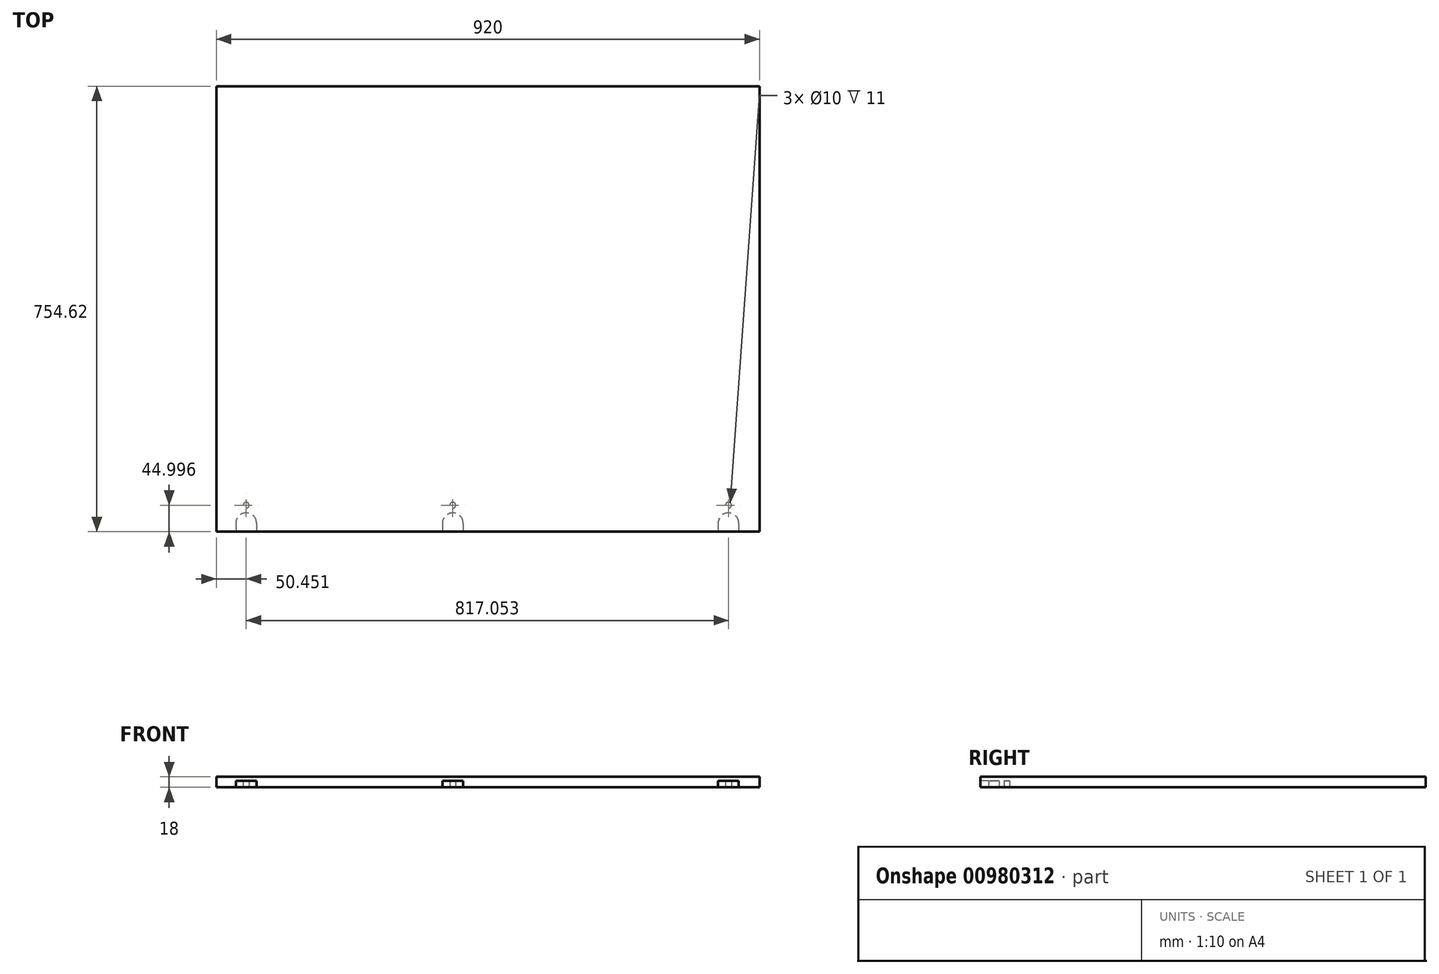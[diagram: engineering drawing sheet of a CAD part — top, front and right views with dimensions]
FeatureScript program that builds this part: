
annotation { "Feature Type Name" : "Feature", "Feature Type Description" : "" }
export const myFeature = defineFeature(function(context is Context, id is Id, definition is map)
    precondition{}
    {
        {
            var Q0;
            Q0=qCreatedBy(makeId("Top.planeOp"),FACE);
            var sketch = newSketch(context, id + "F0", { "sketchPlane" : qUnion([Q0])});
            skLineSegment(sketch, "E0.bottom", {"start": v(-458.88, 406.43) * mm, "end": v(461.12, 406.43) * mm});
            skLineSegment(sketch, "E0.top", {"start": v(-458.88, -348.2) * mm, "end": v(-425.83, -348.2) * mm});
            skLineSegment(sketch, "E0.left", {"start": v(-458.88, 406.43) * mm, "end": v(-458.88, -348.2) * mm});
            skLineSegment(sketch, "E0.right", {"start": v(461.12, 406.43) * mm, "end": v(461.12, -348.2) * mm});
            skArc(sketch, "E1", {"start": v(426.12, -333.7) * mm, "mid": v(408.62, -316.2) * mm, "end": v(391.12, -333.7) * mm});
            skArc(sketch, "E2", {"start": v(-390.88, -333.7) * mm, "mid": v(-408.43, -316.2) * mm, "end": v(-425.88, -333.8) * mm});
            skLineSegment(sketch, "E3", {"start": v(-390.88, -333.7) * mm, "end": v(-390.88, -348.2) * mm});
            skLineSegment(sketch, "E4.trimOffspring", {"start": v(-390.88, -348.2) * mm, "end": v(391.12, -348.2) * mm});
            skLineSegment(sketch, "E5", {"start": v(-425.88, -333.7) * mm, "end": v(-425.83, -348.2) * mm});
            skLineSegment(sketch, "E6", {"start": v(426.12, -333.7) * mm, "end": v(426.12, -348.2) * mm});
            skLineSegment(sketch, "E7", {"start": v(391.12, -333.7) * mm, "end": v(391.12, -348.2) * mm});
            skLineSegment(sketch, "E8.trimOffspring", {"start": v(426.12, -348.2) * mm, "end": v(461.12, -348.2) * mm});
            skCircle(sketch, "E9", {"center": v(-408.43, -303.2) * mm, "radius": 5 * mm});
            skPoint(sketch, "E9.centerSnap0", {"position": v(-408.43, -316.2) * mm});
            skCircle(sketch, "E10", {"center": v(408.62, -303.2) * mm, "radius": 5 * mm});
            skPoint(sketch, "E10.centerSnap0", {"position": v(408.62, -316.2) * mm});
            skSolve(sketch);
        }
        {
            var Q0;
            Q0 = qSketchRegion(id + "F0", true);
            extrude(context, id + "F1", {"entities" : qUnion([Q0]), "depth" : 11 * mm, "offsetDistance" : 25 * mm});
        }
        {
            var Q0;
            Q0=makeQuery(id+"F1.opExtrude","CAP_FACE",FACE,{"disambiguationData":[OSD([sQuery(id+"F0.wireOp",EDGE,"E0.bottom"),sQuery(id+"F0.wireOp",EDGE,"E0.top"),sQuery(id+"F0.wireOp",EDGE,"E0.left"),sQuery(id+"F0.wireOp",EDGE,"E0.right"),sQuery(id+"F0.wireOp",EDGE,"E1"),sQuery(id+"F0.wireOp",EDGE,"E2"),sQuery(id+"F0.wireOp",EDGE,"E3"),sQuery(id+"F0.wireOp",EDGE,"E4.trimOffspring"),sQuery(id+"F0.wireOp",EDGE,"E5"),sQuery(id+"F0.wireOp",EDGE,"E6"),sQuery(id+"F0.wireOp",EDGE,"E7"),sQuery(id+"F0.wireOp",EDGE,"E8.trimOffspring")])],"isStart":false});
            var sketch = newSketch(context, id + "F2", { "sketchPlane" : qUnion([Q0])});
            skLineSegment(sketch, "E11.bottom", {"start": v(-458.88, 406.43) * mm, "end": v(461.12, 406.43) * mm});
            skLineSegment(sketch, "E11.top", {"start": v(-458.88, -348.2) * mm, "end": v(461.12, -348.2) * mm});
            skLineSegment(sketch, "E11.left", {"start": v(-458.88, 406.43) * mm, "end": v(-458.88, -348.2) * mm});
            skLineSegment(sketch, "E11.right", {"start": v(461.12, 406.43) * mm, "end": v(461.12, -348.2) * mm});
            skSolve(sketch);
        }
        {
            var Q0;
            Q0 = qSketchRegion(id + "F2", true);
            extrude(context, id + "F3", {"entities" : qUnion([Q0]), "operationType" : NewBodyOperationType.ADD, "depth" : 7 * mm, "offsetDistance" : 25 * mm});
        }
        {
            var Q0;
            Q0=makeQuery(id+"F1.opExtrude","CAP_FACE",FACE,{"disambiguationData":[OSD([sQuery(id+"F0.wireOp",EDGE,"E0.bottom"),sQuery(id+"F0.wireOp",EDGE,"E0.top"),sQuery(id+"F0.wireOp",EDGE,"E0.left"),sQuery(id+"F0.wireOp",EDGE,"E0.right"),sQuery(id+"F0.wireOp",EDGE,"E1"),sQuery(id+"F0.wireOp",EDGE,"E2"),sQuery(id+"F0.wireOp",EDGE,"E3"),sQuery(id+"F0.wireOp",EDGE,"E4.trimOffspring"),sQuery(id+"F0.wireOp",EDGE,"E5"),sQuery(id+"F0.wireOp",EDGE,"E6"),sQuery(id+"F0.wireOp",EDGE,"E7"),sQuery(id+"F0.wireOp",EDGE,"E8.trimOffspring"),sQuery(id+"F0.wireOp",EDGE,"E9"),sQuery(id+"F0.wireOp",EDGE,"E10")])],"isStart":true});
            var sketch = newSketch(context, id + "F4", { "sketchPlane" : qUnion([Q0])});
            skLineSegment(sketch, "E12", {"start": v(-108.88, 348.2) * mm, "end": v(-108.88, -10.66) * mm});
            skArc(sketch, "E13", {"start": v(-75.88, 333.71) * mm, "mid": v(-58.1, 316.2) * mm, "end": v(-40.89, 334.25) * mm});
            skCircle(sketch, "E14", {"center": v(-58.38, 303.2) * mm, "radius": 5 * mm});
            skLineSegment(sketch, "E15", {"start": v(-40.89, 334.25) * mm, "end": v(-40.89, 348.2) * mm});
            skLineSegment(sketch, "E16", {"start": v(-75.88, 333.71) * mm, "end": v(-75.88, 348.2) * mm});
            skLineSegment(sketch, "E17", {"start": v(-75.88, 348.2) * mm, "end": v(-56.4, 373.66) * mm});
            skLineSegment(sketch, "E18", {"start": v(-56.4, 373.66) * mm, "end": v(-40.89, 348.2) * mm});
            skSolve(sketch);
        }
        {
            var Q0;
            Q0 = qSketchRegion(id + "F4", true);
            extrude(context, id + "F5", {"entities" : qUnion([Q0]), "operationType" : NewBodyOperationType.REMOVE, "oppositeDirection" : true, "depth" : 11 * mm, "offsetDistance" : 25 * mm});
        }
    });
